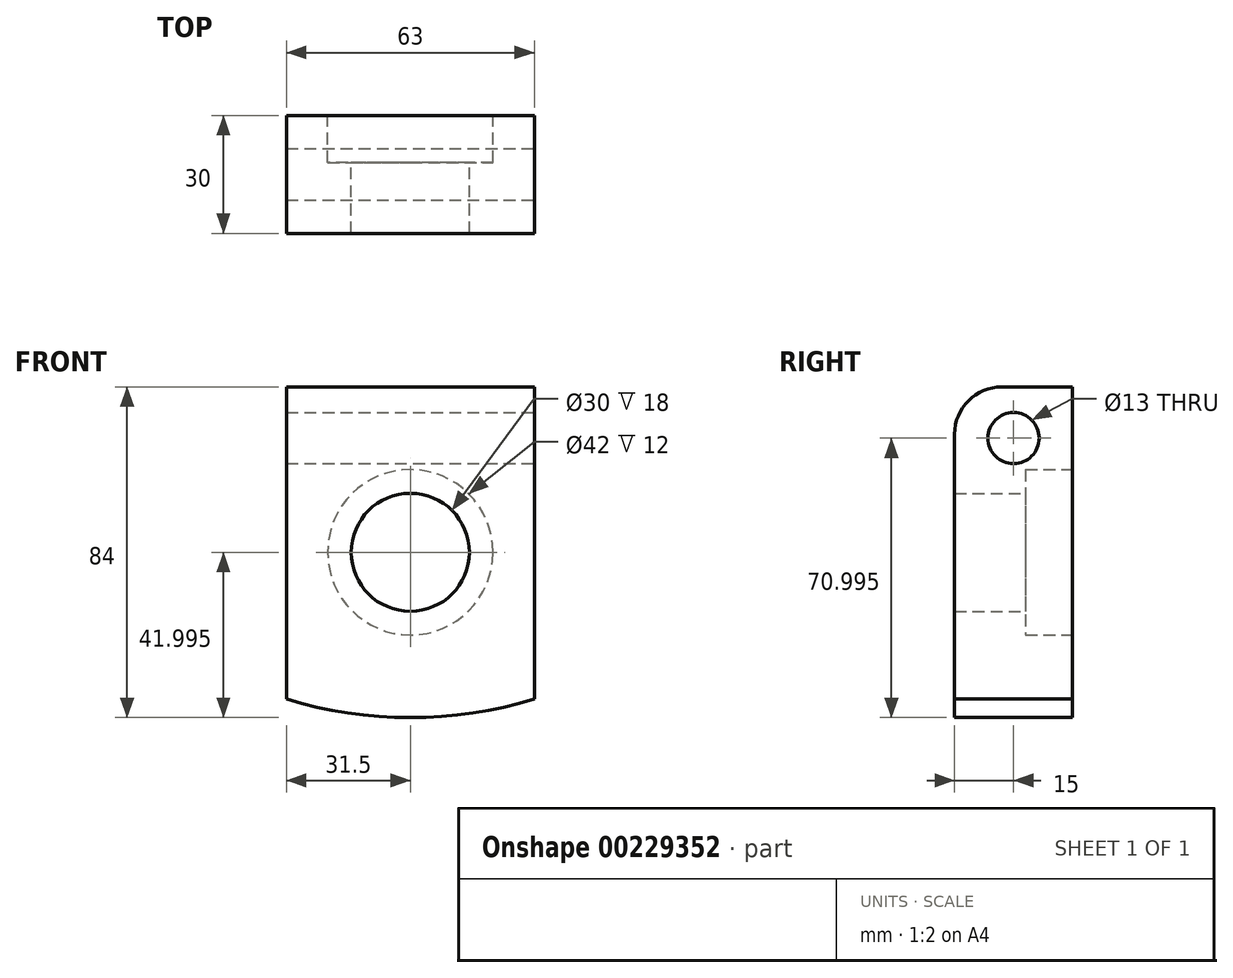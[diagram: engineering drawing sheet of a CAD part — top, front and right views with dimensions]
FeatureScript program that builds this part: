
annotation { "Feature Type Name" : "Feature", "Feature Type Description" : "" }
export const myFeature = defineFeature(function(context is Context, id is Id, definition is map)
    precondition{}
    {
        {
            var Q0;
            Q0=qCreatedBy(makeId("Front.planeOp"),FACE);
            var sketch = newSketch(context, id + "F0", { "sketchPlane" : qUnion([Q0])});
            skLineSegment(sketch, "E0", {"start": v(0, 52.1) * mm, "end": v(0, -31.9) * mm, "construction": true});
            skLineSegment(sketch, "E1.top", {"start": v(-31.5, 52.1) * mm, "end": v(31.5, 52.1) * mm});
            skLineSegment(sketch, "E1.left", {"start": v(-31.5, -27.2) * mm, "end": v(-31.5, 52.1) * mm});
            skLineSegment(sketch, "E1.right", {"start": v(31.5, -27.2) * mm, "end": v(31.5, 52.1) * mm});
            skArc(sketch, "E2", {"start": v(-31.5, -27.2) * mm, "mid": v(0, -31.9) * mm, "end": v(31.5, -27.2) * mm});
            skLineSegment(sketch, "E3", {"start": v(-31.5, 10.1) * mm, "end": v(31.5, 10.1) * mm, "construction": true});
            skSolve(sketch);
        }
        {
            var Q0;
            Q0 = qSketchRegion(id + "F0", true);
            extrude(context, id + "F1", {"entities" : qUnion([Q0]), "depth" : (15 + 15) * mm});
        }
        {
            var Q0;
            Q0=makeQuery(id+"F1.opExtrude","CAP_FACE",FACE,{"disambiguationData":[OSD([sQuery(id+"F0.wireOp",EDGE,"E1.top"),sQuery(id+"F0.wireOp",EDGE,"E1.left"),sQuery(id+"F0.wireOp",EDGE,"E1.right"),sQuery(id+"F0.wireOp",EDGE,"E2")])],"isStart":true});
            var sketch = newSketch(context, id + "F2", { "sketchPlane" : qUnion([Q0])});
            skPoint(sketch, "E4", {"position": v(0, 10.1) * mm});
            skSolve(sketch);
        }
        {
            var Q0;
            Q0=sQuery(id+"F2.wireOp",VERTEX,"E4");
            var Q1;
            Q1=makeQuery(id+"F1.opExtrude","SWEPT_BODY",BODY,{"disambiguationData":[OSD([sQuery(id+"F0.wireOp",EDGE,"E1.top"),sQuery(id+"F0.wireOp",EDGE,"E1.left"),sQuery(id+"F0.wireOp",EDGE,"E1.right"),sQuery(id+"F0.wireOp",EDGE,"E2")])]});
            hole(context, id + "F3", {"style" : HoleStyle.C_BORE, "endStyle" : HoleEndStyle.THROUGH, "holeDiameter" : 30 * mm, "cBoreDiameter" : 42 * mm, "cBoreDepth" : 12 * mm, "startFromSketch" : true, "locations" : qUnion([Q0]), "scope" : qUnion([Q1]), "isTappedThrough" : true});
        }
        {
            var Q0;
            Q0=makeQuery(id+"F1.opExtrude","SWEPT_FACE",FACE,{"disambiguationData":[OSD([sQuery(id+"F0.wireOp",EDGE,"E1.right")])]});
            var sketch = newSketch(context, id + "F4", { "sketchPlane" : qUnion([Q0])});
            skLineSegment(sketch, "E5", {"start": v(-15, 52.1) * mm, "end": v(-15, -27.2) * mm, "construction": true});
            skPoint(sketch, "E6", {"position": v(-15, 39.1) * mm});
            skLineSegment(sketch, "E7", {"start": v(-15, 39.1) * mm, "end": v(-30, 39.1) * mm, "construction": true});
            skSolve(sketch);
        }
        {
            var Q0;
            Q0=makeQuery(id+"F1.opExtrude","CAP_EDGE",EDGE,{"disambiguationData":[OSD([sQuery(id+"F0.wireOp",EDGE,"E1.top")])],"isStart":false});
            fillet(context, id + "F5", {"entities" : qUnion([Q0]), "radius" : 12 * mm, "tangentPropagation" : true, "allowEdgeOverflow" : false});
        }
        {
            var Q0;
            Q0=sQuery(id+"F4.wireOp",VERTEX,"E6");
            var Q1;
            Q1=makeQuery(id+"F1.opExtrude","SWEPT_BODY",BODY,{"disambiguationData":[OSD([sQuery(id+"F0.wireOp",EDGE,"E1.top"),sQuery(id+"F0.wireOp",EDGE,"E1.left"),sQuery(id+"F0.wireOp",EDGE,"E1.right"),sQuery(id+"F0.wireOp",EDGE,"E2")])]});
            hole(context, id + "F6", {"style" : HoleStyle.SIMPLE, "endStyle" : HoleEndStyle.THROUGH, "holeDiameter" : 13 * mm, "startFromSketch" : true, "locations" : qUnion([Q0]), "scope" : qUnion([Q1]), "isTappedThrough" : true});
        }
    });
